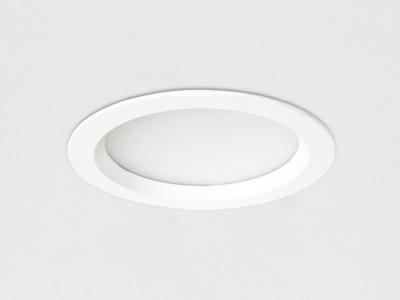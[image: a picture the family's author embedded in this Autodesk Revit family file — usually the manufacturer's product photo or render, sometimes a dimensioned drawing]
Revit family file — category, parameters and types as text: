
# Revit family: DG 1016 MOW
name_source: partatom
category: Lighting Fixtures
revit_build: Autodesk Revit 2017 (Build: 20160225_1515(x64)
units: mm (PartAtom-declared; Revit-internal decimal feet)

## family parameters
Always vertical = Yes
Cut with Voids When Loaded = No
Host = Ceiling
Light Source = Yes
OmniClass Number = 23.80.70.11
OmniClass Title = Luminaries for Internal Lighting
Part Type = Normal
Room Calculation Point = No
Round Connector Dimension = Use Diameter
Shared = No

## types (2) — shared parameters
Color Filter = 16777215
Dimming Lamp Color Temperature Shift = <None>
Emit Shape Visible in Rendering = Yes
Emit from Circle Diameter = 120 mm  [stored 0.393701 ft]
Light Source Symbol Size = 610 mm
Manufacturer = ARLIGHT
Type Image = DG 1016 MOW.jpg
Wattage Comments = 13

## type names (no varying parameters)
- DGMOW.160.13.30
- DGMOW.160.13.40

note: [stored X ft] marks values corroborated as IEEE doubles in the binary element streams (Revit-internal decimal feet)

## geometry (parser evidence)
native form markers: Sweep x2
no freeform markers — native parametric forms only
